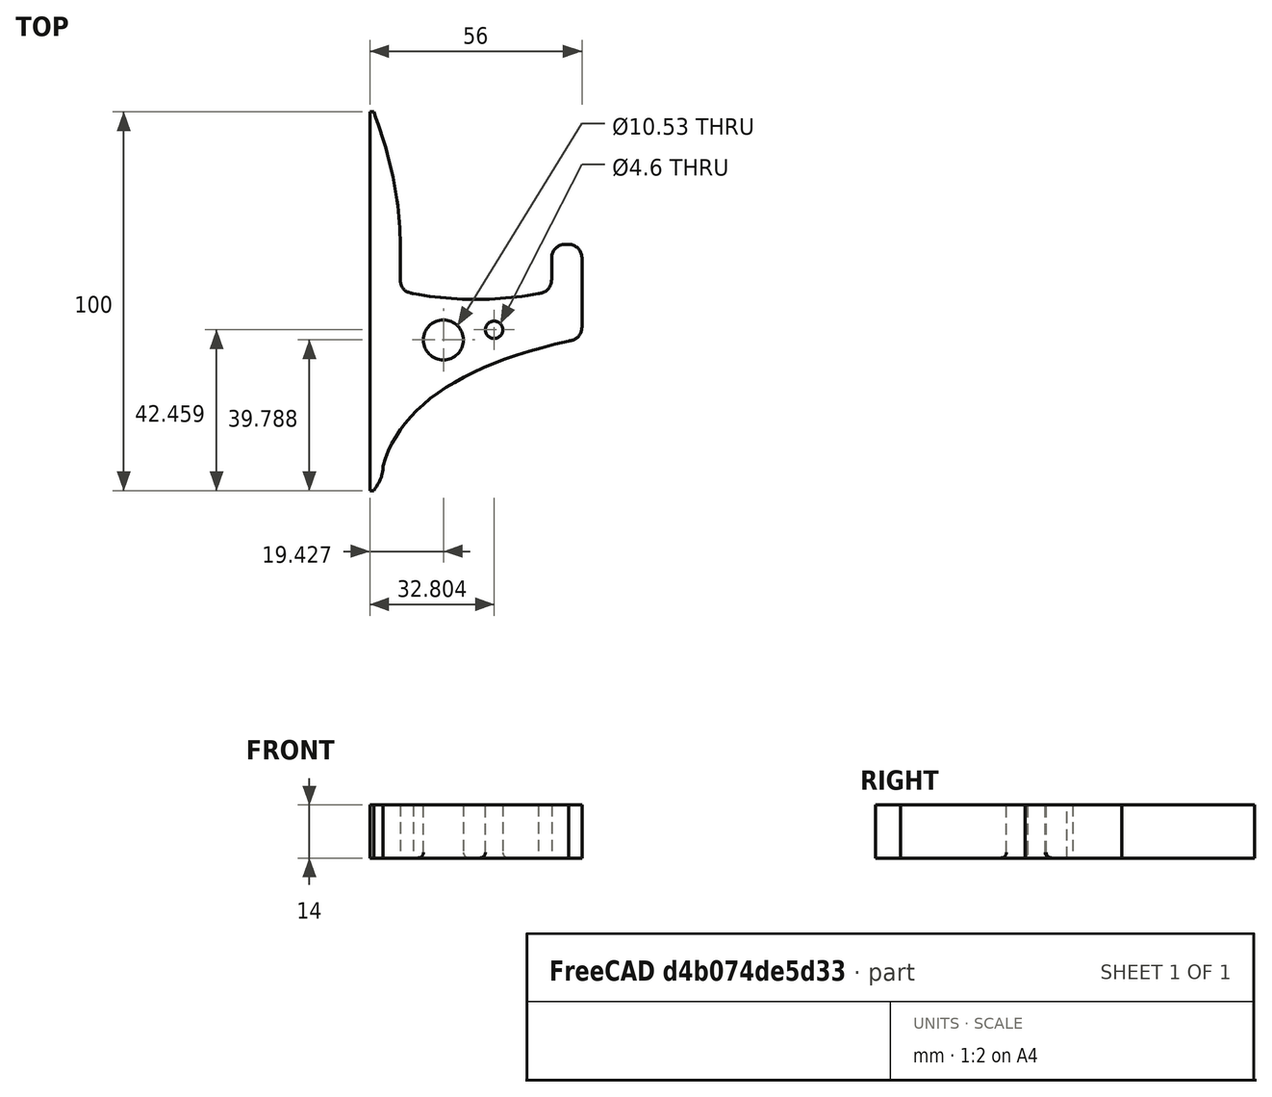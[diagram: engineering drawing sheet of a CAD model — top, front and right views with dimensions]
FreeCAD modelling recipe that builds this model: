
FCSTD DOCUMENT  (FreeCAD 0.19R0.19.2)
Label: headphoneStandWithHookStudsRemovedCurrent_3
License: All rights reserved
LicenseURL: http://en.wikipedia.org/wiki/All_rights_reserved
objects: Part::Fillet×2, Sketcher::SketchObject×1, Part::Extrusion×1, Part::Mirroring×1
note: 5 computed .brp shape members not serialized (recipe doc carries the construction recipe); baked Part::Feature solids carry a one-line shape summary decoded from their .brp

FEATURE [Sketcher::SketchObject] Sketch
  FullyConstrained = false
  sketch-geometry (51):
    g0: LineSegment StartX=0 StartY=0 StartZ=0 EndX=0 EndY=100 EndZ=0
    g1: LineSegment StartX=8 StartY=65 StartZ=0 EndX=8 EndY=56 EndZ=0
    g2: Circle CenterX=8 CenterY=56 CenterZ=0 NormalX=0 NormalY=0 NormalZ=1 AngleXU=0 Radius=1
    g3: Circle CenterX=8 CenterY=52.5 CenterZ=0 NormalX=0 NormalY=0 NormalZ=1 AngleXU=0 Radius=1
    g4: Circle CenterX=11.5 CenterY=52 CenterZ=0 NormalX=0 NormalY=0 NormalZ=1 AngleXU=0 Radius=1
    g5: BSplineCurve PolesCount=3 KnotsCount=2 Degree=2 IsPeriodic=0
    g6: GeomPoint X=8 Y=56 Z=0
    g7: GeomPoint X=11.5 Y=52 Z=0
    g8: Circle CenterX=44.5 CenterY=52 CenterZ=0 NormalX=0 NormalY=0 NormalZ=1 AngleXU=0 Radius=1
    g9: Circle CenterX=48 CenterY=52.5 CenterZ=0 NormalX=0 NormalY=0 NormalZ=1 AngleXU=0 Radius=1
    g10: Circle CenterX=48 CenterY=56 CenterZ=0 NormalX=0 NormalY=0 NormalZ=1 AngleXU=0 Radius=1
    g11: BSplineCurve PolesCount=3 KnotsCount=2 Degree=2 IsPeriodic=0
    g12: GeomPoint X=44.5 Y=52 Z=0
    g13: GeomPoint X=48 Y=56 Z=0
    g14: Circle CenterX=11.5 CenterY=52 CenterZ=0 NormalX=0 NormalY=0 NormalZ=1 AngleXU=0 Radius=1
    g15: Circle CenterX=28 CenterY=49 CenterZ=0 NormalX=0 NormalY=0 NormalZ=1 AngleXU=0 Radius=1
    g16: Circle CenterX=44.5 CenterY=52 CenterZ=0 NormalX=0 NormalY=0 NormalZ=1 AngleXU=0 Radius=1
    g17: BSplineCurve PolesCount=3 KnotsCount=2 Degree=2 IsPeriodic=0
    g18: GeomPoint X=11.5 Y=52 Z=0
    g19: GeomPoint X=44.5 Y=52 Z=0
    g20: LineSegment StartX=48 StartY=65 StartZ=0 EndX=48 EndY=56 EndZ=0
    g21: LineSegment StartX=48 StartY=65 StartZ=0 EndX=56 EndY=65 EndZ=0
    g22: LineSegment StartX=56 StartY=65 StartZ=0 EndX=56 EndY=43.5 EndZ=0
    g23: Circle CenterX=56 CenterY=43.5 CenterZ=0 NormalX=0 NormalY=0 NormalZ=1 AngleXU=0 Radius=1
    g24: Circle CenterX=56 CenterY=40 CenterZ=0 NormalX=0 NormalY=0 NormalZ=1 AngleXU=0 Radius=1
    g25: Circle CenterX=52.5 CenterY=39.5 CenterZ=0 NormalX=0 NormalY=0 NormalZ=1 AngleXU=0 Radius=1
    g26: BSplineCurve PolesCount=3 KnotsCount=2 Degree=2 IsPeriodic=0
    g27: GeomPoint X=56 Y=43.5 Z=0
    g28: GeomPoint X=52.5 Y=39.5 Z=0
    g29: LineSegment StartX=0 StartY=0 StartZ=0 EndX=1 EndY=0 EndZ=0
    g30: LineSegment StartX=0 StartY=100 StartZ=0 EndX=1 EndY=100 EndZ=0
    g31: Circle CenterX=8 CenterY=65 CenterZ=0 NormalX=0 NormalY=0 NormalZ=1 AngleXU=0 Radius=1
    g32: Circle CenterX=8 CenterY=81.5 CenterZ=0 NormalX=0 NormalY=0 NormalZ=1 AngleXU=0 Radius=1
    g33: Circle CenterX=1 CenterY=100 CenterZ=0 NormalX=0 NormalY=0 NormalZ=1 AngleXU=0 Radius=1
    g34: BSplineCurve PolesCount=3 KnotsCount=2 Degree=2 IsPeriodic=0
    g35: GeomPoint X=8 Y=65 Z=0
    g36: GeomPoint X=1 Y=100 Z=0
    g37: Circle CenterX=1 CenterY=0 CenterZ=0 NormalX=0 NormalY=0 NormalZ=1 AngleXU=0 Radius=1
    g38: Circle CenterX=3.5 CenterY=3.3 CenterZ=0 NormalX=0 NormalY=0 NormalZ=1 AngleXU=0 Radius=1
    g39: Circle CenterX=3.5 CenterY=6.5 CenterZ=0 NormalX=0 NormalY=0 NormalZ=1 AngleXU=0 Radius=1
    g40: BSplineCurve PolesCount=3 KnotsCount=2 Degree=2 IsPeriodic=0
    g41: GeomPoint X=1 Y=0 Z=0
    g42: GeomPoint X=3.5 Y=6.5 Z=0
    g43: Circle CenterX=52.5 CenterY=39.5 CenterZ=0 NormalX=0 NormalY=0 NormalZ=1 AngleXU=0 Radius=1
    g44: Circle CenterX=10 CenterY=30 CenterZ=0 NormalX=0 NormalY=0 NormalZ=1 AngleXU=0 Radius=1
    g45: Circle CenterX=3.5 CenterY=6.5 CenterZ=0 NormalX=0 NormalY=0 NormalZ=1 AngleXU=0 Radius=1
    g46: BSplineCurve PolesCount=3 KnotsCount=2 Degree=2 IsPeriodic=0
    g47: GeomPoint X=52.5 Y=39.5 Z=0
    g48: GeomPoint X=3.5 Y=6.5 Z=0
    g49: Circle CenterX=19.4268 CenterY=39.7877 CenterZ=0 NormalX=0 NormalY=0 NormalZ=1 AngleXU=0 Radius=5.26565
    g50: Circle CenterX=32.8037 CenterY=42.4589 CenterZ=0 NormalX=0 NormalY=0 NormalZ=1 AngleXU=0 Radius=2.29927
  constraints (92):
    c: Vertical(g0)
    c: Distance(g0) = 100
    c: Coincident(g0,g-1)
    c: Block(g0)
    c: Vertical(g1)
    c: Distance(g1) = 9
    c: Block(g1)
    c: Weight(g2) = 1
    c: Equal(g2,g3)
    c: Equal(g2,g4)
    c: InternalAlignment(g2,g5)
    c: InternalAlignment(g3,g5)
    c: InternalAlignment(g4,g5)
    c: InternalAlignment(g6,g5)
    c: InternalAlignment(g7,g5)
    c: Coincident(g5,g1)
    c: Block(g5)
    c: Weight(g8) = 1
    c: Equal(g8,g9)
    c: Equal(g8,g10)
    c: InternalAlignment(g8,g11)
    c: InternalAlignment(g9,g11)
    c: InternalAlignment(g10,g11)
    c: InternalAlignment(g12,g11)
    c: InternalAlignment(g13,g11)
    c: Block(g11)
    c: Weight(g14) = 1
    c: Equal(g14,g15)
    c: Equal(g14,g16)
    c: InternalAlignment(g14,g17)
    c: InternalAlignment(g15,g17)
    c: InternalAlignment(g16,g17)
    c: InternalAlignment(g18,g17)
    c: InternalAlignment(g19,g17)
    c: Coincident(g17,g5)
    c: Coincident(g17,g11)
    c: Block(g17)
    c: Vertical(g20)
    c: Coincident(g20,g11)
    c: Equal(g1,g20)
    c: Horizontal(g21)
    c: Coincident(g21,g20)
    c: Distance(g21) = 8
    c: Vertical(g22)
    c: Block(g21)
    c: Coincident(g22,g21)
    c: Distance(g22) = 21.5
    c: Weight(g23) = 1
    c: Equal(g23,g24)
    c: Equal(g23,g25)
    c: InternalAlignment(g23,g26)
    c: InternalAlignment(g24,g26)
    c: InternalAlignment(g25,g26)
    c: InternalAlignment(g27,g26)
    c: InternalAlignment(g28,g26)
    c: Coincident(g26,g22)
    c: Block(g26)
    c: Horizontal(g29)
    c: Distance(g29) = 1
    c: Coincident(g29,g0)
    c: Block(g29)
    c: Horizontal(g30)
    c: Distance(g30) = 1
    c: Coincident(g30,g0)
    c: Block(g30)
    c: Weight(g31) = 1
    c: Equal(g31,g32)
    c: Equal(g31,g33)
    c: InternalAlignment(g31,g34)
    c: InternalAlignment(g32,g34)
    c: InternalAlignment(g33,g34)
    c: InternalAlignment(g35,g34)
    c: InternalAlignment(g36,g34)
    c: Coincident(g34,g30)
    c: Coincident(g34,g1)
    c: Block(g34)
    c: Weight(g37) = 1
    c: Equal(g37,g38)
    c: Equal(g37,g39)
    c: InternalAlignment(g37,g40)
    c: InternalAlignment(g38,g40)
    c: InternalAlignment(g39,g40)
    c: InternalAlignment(g41,g40)
    c: InternalAlignment(g44,g46)
    c: InternalAlignment(g45,g46)
    c: InternalAlignment(g47,g46)
    c: InternalAlignment(g48,g46)
    c: Coincident(g46,g40)
    c: Coincident(g46,g26)
    c: Block(g46)
    c: Block(g49)
    c: Block(g50)
FEATURE [Part::Extrusion] Extrude
  Base = -> Sketch
  Dir = (0,0,1)
  DirMode = 2
  FaceMakerClass = Part::FaceMakerBullseye
  LengthFwd = 14
  LengthRev = 0
  Solid = true
  Symmetric = false
FEATURE [Part::Fillet] Fillet
  Base = -> Extrude
  Edges = 2 edges r=3.5: [Edge26,Edge29]
FEATURE [Part::Fillet] Fillet001
  Base = -> Fillet
  Edges = 2 edges r=1.5: [Edge39,Edge40]
FEATURE [Part::Mirroring] Part__Mirroring  label="Fillet001 (Mirror #1)"
  Base = (0,0,0)
  Normal = (0,0,1)
  Source = -> Fillet001
